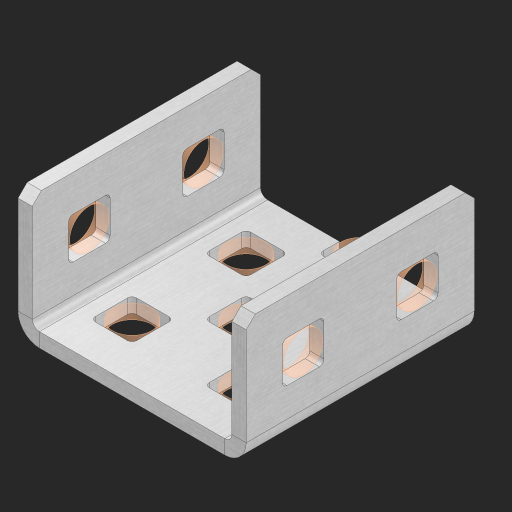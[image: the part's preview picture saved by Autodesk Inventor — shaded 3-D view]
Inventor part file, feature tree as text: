
AUTODESK INVENTOR PART (.ipt)
format: ipt  version: 2023 (Build 270158000, 158)  size: 586,240 bytes
history: native  units: in
note: dims shown in document units (in); Inventor stores cm internally (conversion verified against a paired STEP export)
features: other x17, sheet_metal_op x11, sketch x10, extrude x8, pattern_linear x2, mirror x1, chamfer x1
ambient origin geometry x8: Origin, YZ Plane, XZ Plane, XY Plane, X Axis, Y Axis, Z Axis, Center Point
bodies: Solid1 (feature_tree), Body (feature_tree)
feature tree (50):
  sheet_metal_op  "Flanges"
  other  "Flange Pattern Plane"
  other  "Flange Pattern Sketch"
  sheet_metal_op  "Flange Pattern"
  sheet_metal_op  "Body Pattern"
  pattern_linear  "Center Pattern"  Spacing1=0.0625in  [1 undecoded]
  other  "Arc Length"
  mirror  "Notch Mirror"
  pattern_linear  "Notch Pattern"  Spacing1=0.182in  [1 undecoded]
  chamfer  "End Chamfer"
  extrude  "Half Cut"  Depth=0.02in
  sketch  "Sketch1"  dims[d0=1.0in]
  other  "Plate1"
  sketch  "Sketch2"  dims[d1=1.0in]
  other  "Plate2"
  sheet_metal_op  "Bend1"
  sheet_metal_op  "Corner1"
  sketch  "Sketch3"  dims[d2=0.0625in]
  sketch  "Sketch7"  dims[d3=0.0625in]
  other  "Srf1"
  other  "Srf2"
  sketch  "Sketch8"  dims[d4=0.0312in]
  sketch  "Sketch9"  dims[d5=0.125in]
  other  "Srf91"
  sheet_metal_op  "Body Pattern Sketch"
  other  "Srf92"
  sketch  "Sketch13"  dims[d6=0.0625in]
  sketch  "Sketch14"  dims[d7=0.5in d8=90.0deg d9=0.0312in]
  sketch  "Sketch15"  dims[d10=0.25in]
  sketch  "Sketch16"  dims[d11=0.0625in d12=0.0625in d16=0.182in d17=0.02in d18=0.0625in d19=0.0in d20=0.25in d21=0.25in d38=0.7874in d40=0.5in d41=0.7874in d43=1.0in d46=0.172in d47=1.0in d48=0.0in d49=0.182in d50=0.02in d51=0.25in d52=0.25in d53=0.0625in d54=0.0in d55=0.172in d56=1.0in d57=0.0in d58=0.25in d60=0.7874in d62=0.5in d63=0.7874in d65=0.5in d85=0.1473in d86=0.1782in d88=0.04in d89=0.0625in d90=0.0in d91=0.04in d92=0.0491in d95=2.5in d96=0.04in d97=0.25in d98=45.0deg d99=0.25in d100=0.5in d101=0.0in d102=2.497in d106=0.182in d107=0.02in d108=0.5in d109=0.5in d110=0.0625in d111=0.0in d112=0.172in d113=0.5in d114=0.0in d117=0.5in d118=0.5in d119=0.5in]
  other  "Srf786"
  other  "Srf823"
  other  "Srf824"
  other  "Srf856"
  other  "Srf857"
  other  "Srf889"
  sheet_metal_op  "Flange Stamp"
  sheet_metal_op  "Flange Circle"
  sheet_metal_op  "Body Stamp"
  sheet_metal_op  "Body Circle"
  other  "Center Stamp"
  other  "Center Circle"
  sheet_metal_op  "Notch"
  extrude  "ExtrusionSrf2"  Depth=0.0625in
  extrude  "ExtrusionSrf92"  TaperAngle=0.0deg  [1 undecoded]
  extrude  "ExtrusionSrf823"  Depth=0.25in
  extrude  "ExtrusionSrf824"  Depth=0.25in
  extrude  "ExtrusionSrf856"  Depth=0.5in
  extrude  "ExtrusionSrf857"  Depth=0.5in
  extrude  "ExtrusionSrf889"  Depth=1.0in TaperAngle=0.0deg
note: 3 required parameter values undecoded (feature->parameter linkage not recoverable at this tier; creation-order binding heuristic only, values carry confidence <= 0.55)
